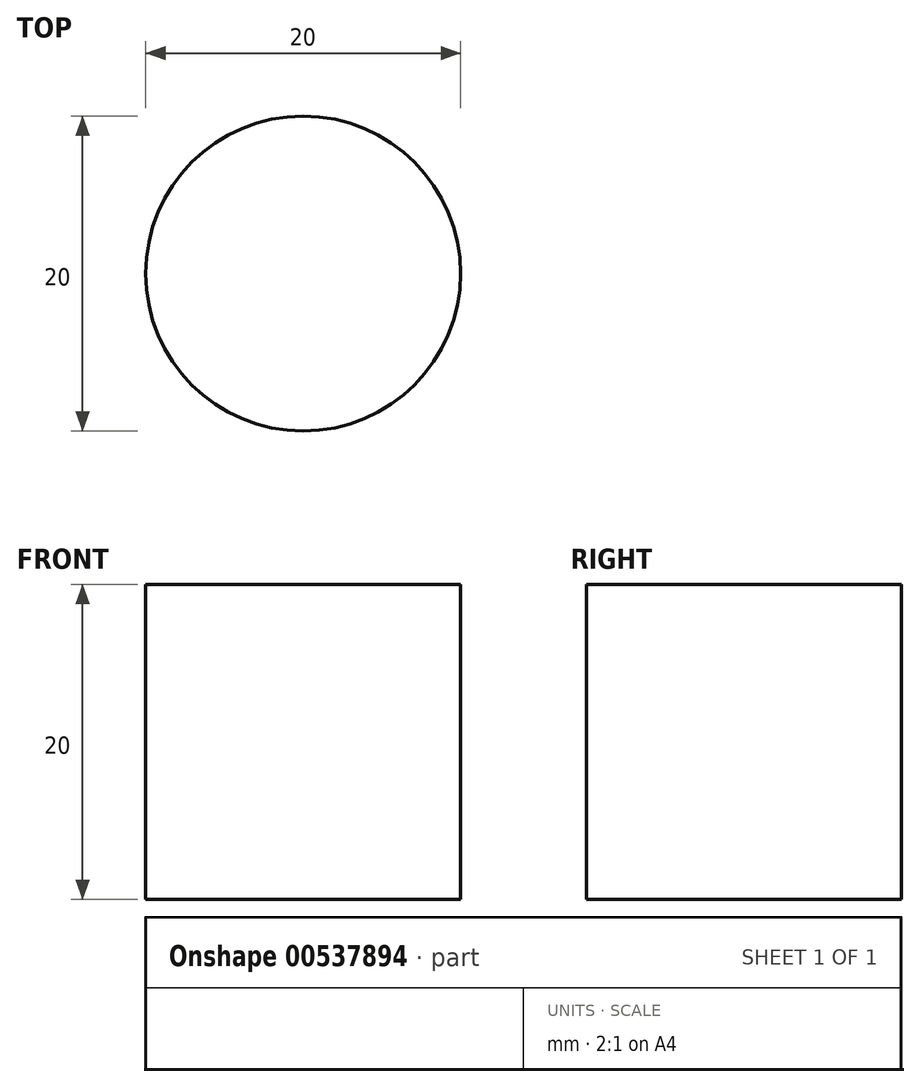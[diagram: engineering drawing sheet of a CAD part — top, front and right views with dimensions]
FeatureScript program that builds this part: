
annotation { "Feature Type Name" : "Feature", "Feature Type Description" : "" }
export const myFeature = defineFeature(function(context is Context, id is Id, definition is map)
    precondition{}
    {
        {
            var Q0;
            Q0=qCreatedBy(makeId("Top.planeOp"),FACE);
            var sketch = newSketch(context, id + "F0", { "sketchPlane" : qUnion([Q0])});
            skCircle(sketch, "E0", {"center": v(0, 0) * mm, "radius": 10 * mm});
            skSolve(sketch);
        }
        {
            var Q0;
            Q0=makeQuery(id+"F0.imprint","IMPRINT",FACE,{"disambiguationData":[TD([[makeQuery(id+"F0.imprint","IMPRINT",EDGE,{"derivedFrom":sQuery(id+"F0.wireOp",EDGE,"E0")}),1.0]])]});
            extrude(context, id + "F1", {"entities" : qUnion([Q0]), "depth" : 20 * mm, "offsetDistance" : 25.4 * mm});
        }
    });
